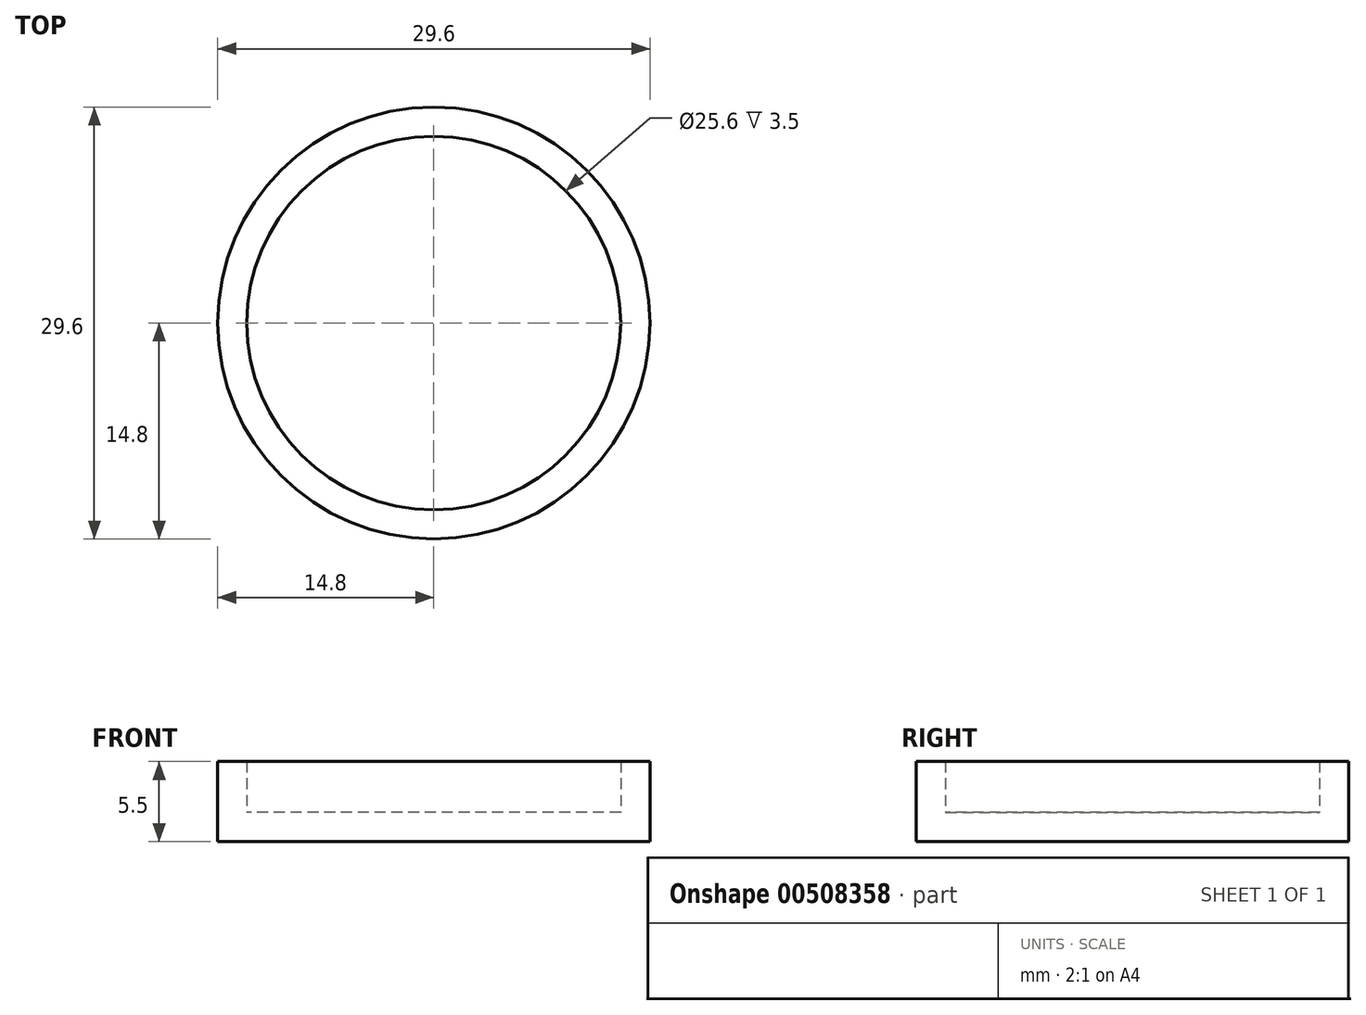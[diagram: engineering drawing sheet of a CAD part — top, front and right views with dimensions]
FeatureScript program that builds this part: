
annotation { "Feature Type Name" : "Feature", "Feature Type Description" : "" }
export const myFeature = defineFeature(function(context is Context, id is Id, definition is map)
    precondition{}
    {
        {
            var Q0;
            Q0=qCreatedBy(makeId("Top.planeOp"),FACE);
            var sketch = newSketch(context, id + "F0", { "sketchPlane" : qUnion([Q0])});
            skCircle(sketch, "E0", {"center": v(0, 0) * mm, "radius": 12.8 * mm});
            skCircle(sketch, "E1", {"center": v(0, 0) * mm, "radius": 14.8 * mm});
            skSolve(sketch);
        }
        {
            var Q0;
            Q0=makeQuery(id+"F0.imprint","IMPRINT",FACE,{"disambiguationData":[TD([[makeQuery(id+"F0.imprint","IMPRINT",EDGE,{"derivedFrom":sQuery(id+"F0.wireOp",EDGE,"E0")}),-1.0]])]});
            extrude(context, id + "F1", {"entities" : qUnion([Q0]), "depth" : 3.5 * mm, "offsetDistance" : 25 * mm});
        }
        {
            var Q0;
            Q0=makeQuery(id+"F1.opExtrude","CAP_FACE",FACE,{"disambiguationData":[OSD([sQuery(id+"F0.wireOp",EDGE,"E0"),sQuery(id+"F0.wireOp",EDGE,"E1")])],"isStart":true});
            var sketch = newSketch(context, id + "F2", { "sketchPlane" : qUnion([Q0])});
            skCircle(sketch, "E2", {"center": v(0, 0) * mm, "radius": 14.8 * mm});
            skSolve(sketch);
        }
        {
            var Q0;
            Q0 = qSketchRegion(id + "F2", true);
            extrude(context, id + "F3", {"entities" : qUnion([Q0]), "operationType" : NewBodyOperationType.ADD, "depth" : 2 * mm, "offsetDistance" : 25 * mm});
        }
    });
